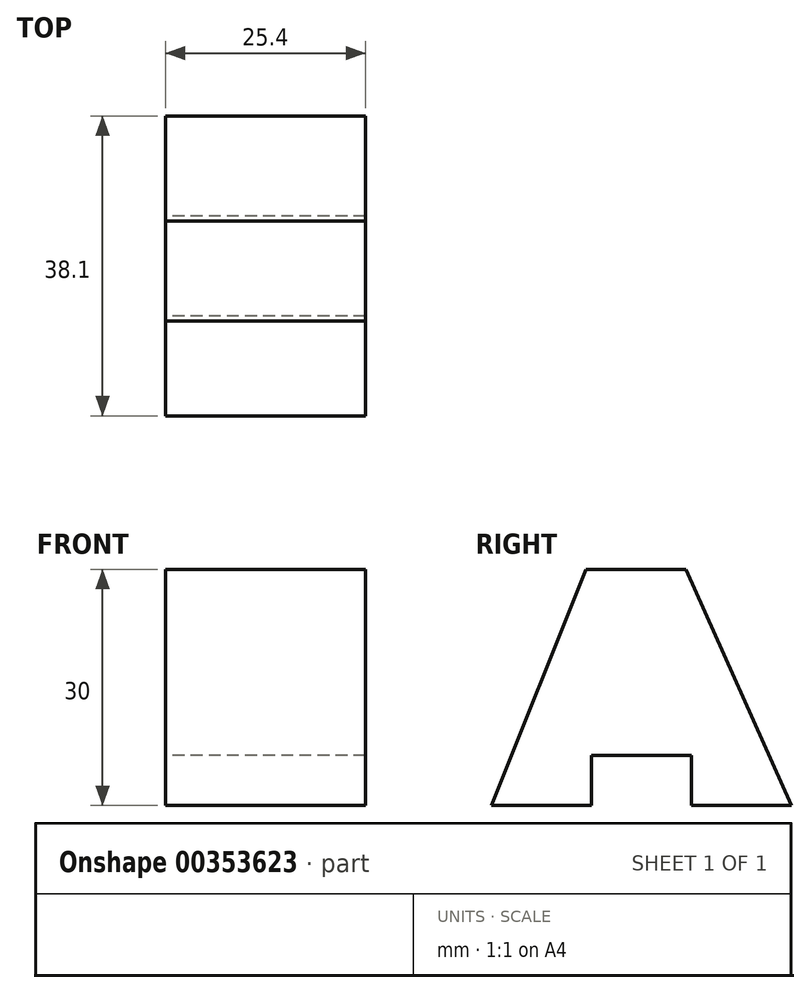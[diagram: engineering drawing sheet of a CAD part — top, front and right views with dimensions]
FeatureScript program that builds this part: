
annotation { "Feature Type Name" : "Feature", "Feature Type Description" : "" }
export const myFeature = defineFeature(function(context is Context, id is Id, definition is map)
    precondition{}
    {
        {
            var Q0;
            Q0=qCreatedBy(makeId("Right.planeOp"),FACE);
            var sketch = newSketch(context, id + "F0", { "sketchPlane" : qUnion([Q0])});
            skLineSegment(sketch, "E0", {"start": v(0, 0) * mm, "end": v(12.7, 0) * mm});
            skLineSegment(sketch, "E1", {"start": v(12.7, 0) * mm, "end": v(12.7, 6.35) * mm});
            skLineSegment(sketch, "E2", {"start": v(12.7, 6.35) * mm, "end": v(25.4, 6.35) * mm});
            skLineSegment(sketch, "E3", {"start": v(25.4, 6.35) * mm, "end": v(25.4, 0) * mm});
            skLineSegment(sketch, "E4", {"start": v(25.4, 0) * mm, "end": v(38.1, 0) * mm});
            skLineSegment(sketch, "E5", {"start": v(38.1, 0) * mm, "end": v(24.73, 30) * mm});
            skLineSegment(sketch, "E6", {"start": v(24.73, 30) * mm, "end": v(12.03, 30) * mm});
            skLineSegment(sketch, "E7", {"start": v(12.03, 30) * mm, "end": v(0, 0) * mm});
            skSolve(sketch);
        }
        {
            var Q0;
            Q0=makeQuery(id+"F0.imprint","IMPRINT",FACE,{"disambiguationData":[TD([[makeQuery(id+"F0.imprint","IMPRINT",EDGE,{"derivedFrom":sQuery(id+"F0.wireOp",EDGE,"E0")}),1.0]])]});
            extrude(context, id + "F1", {"entities" : qUnion([Q0]), "depth" : 25.4 * mm});
        }
    });
